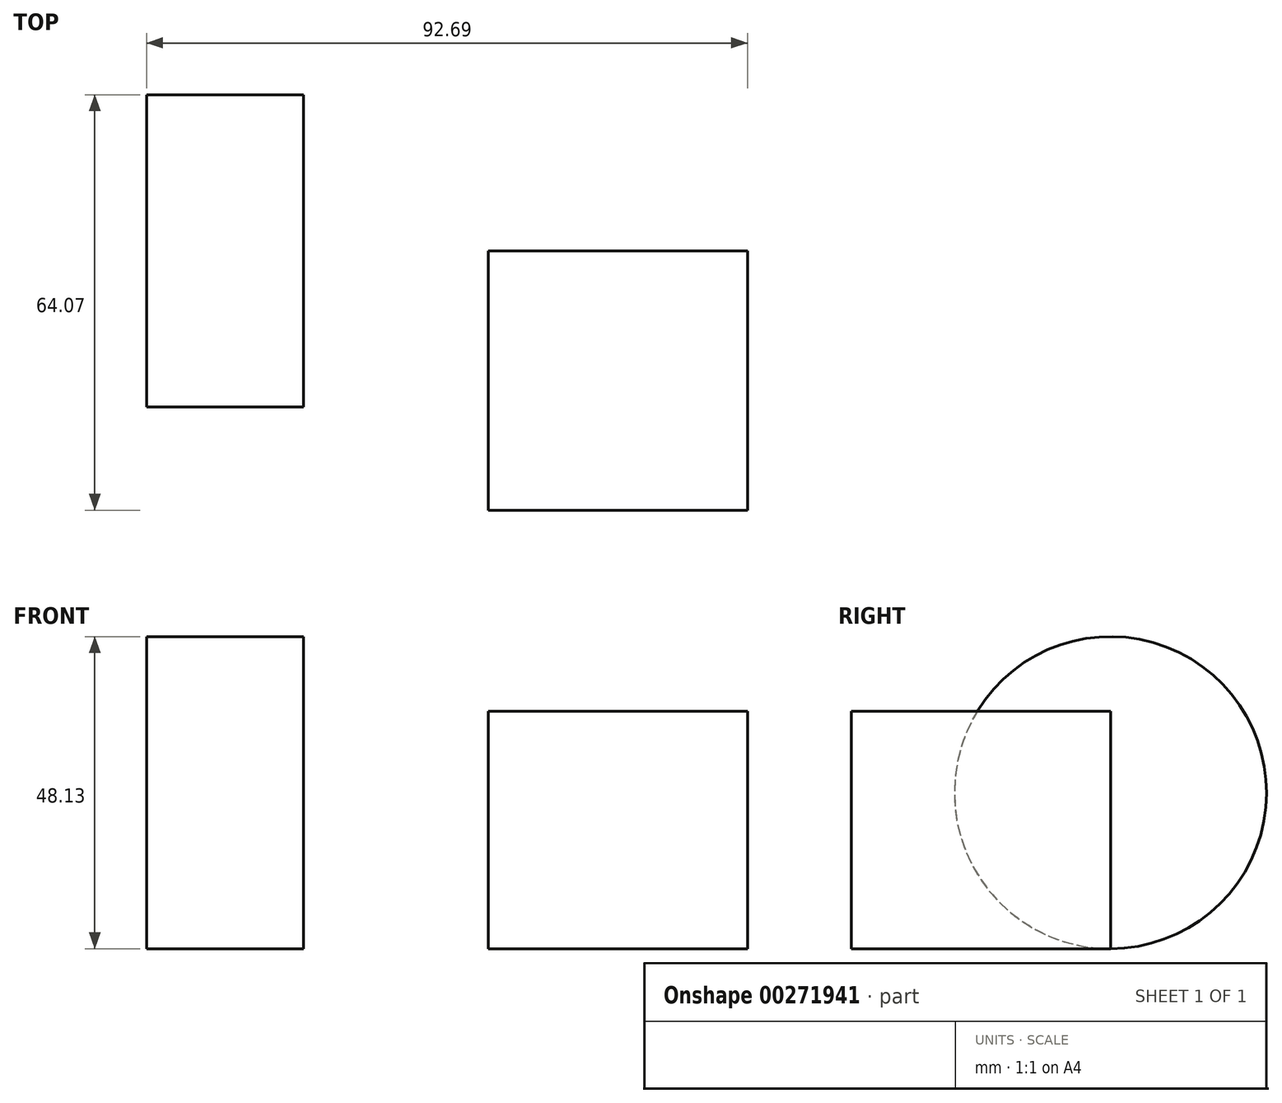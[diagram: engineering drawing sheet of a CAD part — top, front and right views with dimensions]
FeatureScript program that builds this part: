
annotation { "Feature Type Name" : "Feature", "Feature Type Description" : "" }
export const myFeature = defineFeature(function(context is Context, id is Id, definition is map)
    precondition{}
    {
        {
            var Q0;
            Q0=qCreatedBy(makeId("Front.planeOp"),FACE);
            var sketch = newSketch(context, id + "F0", { "sketchPlane" : qUnion([Q0])});
            skLineSegment(sketch, "E0", {"start": v(0, 0) * mm, "end": v(40, 0) * mm});
            skLineSegment(sketch, "E1", {"start": v(40, 0) * mm, "end": v(40, 36.62) * mm});
            skLineSegment(sketch, "E2", {"start": v(40, 36.62) * mm, "end": v(0, 36.62) * mm});
            skLineSegment(sketch, "E3", {"start": v(0, 36.62) * mm, "end": v(0, 0) * mm});
            skSolve(sketch);
        }
        {
            var Q0;
            Q0 = qSketchRegion(id + "F0", true);
            extrude(context, id + "F1", {"entities" : qUnion([Q0]), "depth" : 40 * mm});
        }
        {
            var Q0;
            Q0=qCreatedBy(makeId("Front.planeOp"),FACE);
            var sketch = newSketch(context, id + "F2", { "sketchPlane" : qUnion([Q0])});
            skLineSegment(sketch, "E4", {"start": v(-28.48, 0) * mm, "end": v(-28.48, 24.07) * mm});
            skLineSegment(sketch, "E5", {"start": v(-28.48, 24.07) * mm, "end": v(-52.69, 24.07) * mm});
            skLineSegment(sketch, "E6", {"start": v(-52.69, 24.07) * mm, "end": v(-52.69, 0) * mm});
            skLineSegment(sketch, "E7", {"start": v(-52.69, 0) * mm, "end": v(-28.48, 0) * mm});
            skLineSegment(sketch, "E8", {"start": v(-52.69, 24.07) * mm, "end": v(-70.06, 24.07) * mm, "construction": true});
            skSolve(sketch);
        }
        {
            var Q0;
            Q0 = qSketchRegion(id + "F2", true);
            var Q1;
            Q1=sQuery(id+"F2.wireOp",EDGE,"E8");
            revolve(context, id + "F3", {"entities" : qUnion([Q0]), "axis" : qUnion([Q1]), "revolveType" : RevolveType.FULL});
        }
    });
